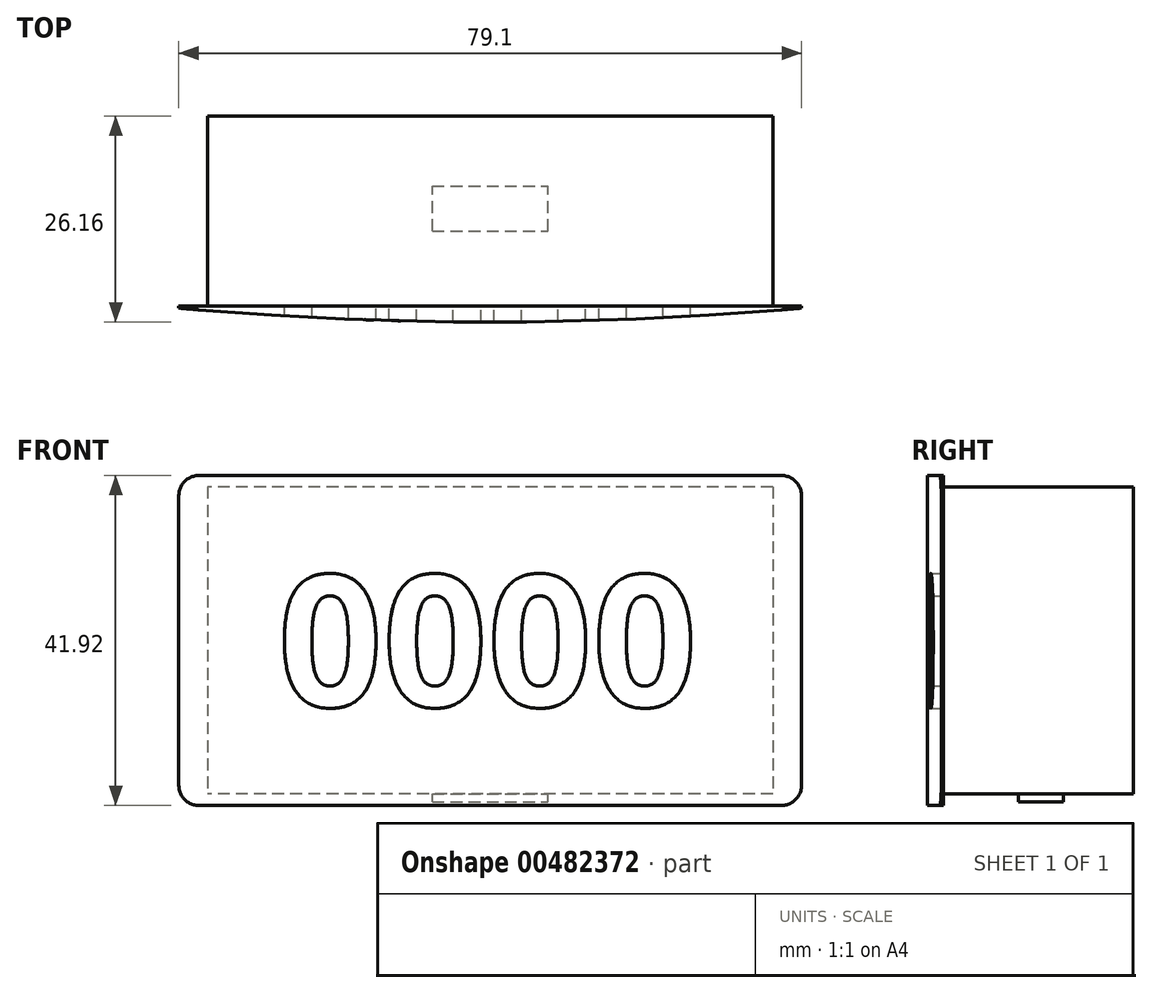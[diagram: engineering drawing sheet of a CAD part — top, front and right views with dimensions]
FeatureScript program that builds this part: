
annotation { "Feature Type Name" : "Feature", "Feature Type Description" : "" }
export const myFeature = defineFeature(function(context is Context, id is Id, definition is map)
    precondition{}
    {
        {
            var Q0;
            Q0=qCreatedBy(makeId("Front.planeOp"),FACE);
            var sketch = newSketch(context, id + "F0", { "sketchPlane" : qUnion([Q0])});
            skLineSegment(sketch, "E0.bottom", {"start": v(-39.55, 20.95) * mm, "end": v(39.55, 20.95) * mm});
            skLineSegment(sketch, "E0.top", {"start": v(-39.55, -20.96) * mm, "end": v(39.55, -20.96) * mm});
            skLineSegment(sketch, "E0.left", {"start": v(-39.55, 20.95) * mm, "end": v(-39.55, -20.96) * mm});
            skLineSegment(sketch, "E0.right", {"start": v(39.55, 20.95) * mm, "end": v(39.55, -20.96) * mm});
            skPoint(sketch, "E0.middle", {"position": v(0, 0) * mm});
            skSolve(sketch);
        }
        {
            var Q0;
            Q0 = qSketchRegion(id + "F0", true);
            extrude(context, id + "F1", {"entities" : qUnion([Q0]), "depth" : 2.03 * mm});
        }
        {
            var Q0;
            Q0=makeQuery(id+"F1.opExtrude","SWEPT_FACE",FACE,{"disambiguationData":[OSD([sQuery(id+"F0.wireOp",EDGE,"E0.top")])]});
            var sketch = newSketch(context, id + "F2", { "sketchPlane" : qUnion([Q0])});
            skCircle(sketch, "E1", {"center": v(0, -442.47) * mm, "radius": 444.5 * mm});
            skSolve(sketch);
        }
        {
            var Q0;
            Q0 = qSketchRegion(id + "F2", true);
            extrude(context, id + "F3", {"entities" : qUnion([Q0]), "operationType" : NewBodyOperationType.INTERSECT, "oppositeDirection" : true, "depth" : 50.8 * mm});
        }
        {
            var Q0;
            Q0=makeQuery(id+"F1.opExtrude","CAP_FACE",FACE,{"disambiguationData":[OSD([sQuery(id+"F0.wireOp",EDGE,"E0.bottom"),sQuery(id+"F0.wireOp",EDGE,"E0.top"),sQuery(id+"F0.wireOp",EDGE,"E0.left"),sQuery(id+"F0.wireOp",EDGE,"E0.right")])],"isStart":true});
            var sketch = newSketch(context, id + "F4", { "sketchPlane" : qUnion([Q0])});
            skLineSegment(sketch, "E2.bottom", {"start": v(-35.92, 19.5) * mm, "end": v(35.92, 19.5) * mm});
            skLineSegment(sketch, "E2.top", {"start": v(-35.92, -19.5) * mm, "end": v(35.92, -19.5) * mm});
            skLineSegment(sketch, "E2.left", {"start": v(-35.92, 19.5) * mm, "end": v(-35.92, -19.5) * mm});
            skLineSegment(sketch, "E2.right", {"start": v(35.92, 19.5) * mm, "end": v(35.92, -19.5) * mm});
            skPoint(sketch, "E2.middle", {"position": v(0, 0) * mm});
            skSolve(sketch);
        }
        {
            var Q0;
            Q0 = qSketchRegion(id + "F4", true);
            extrude(context, id + "F5", {"entities" : qUnion([Q0]), "operationType" : NewBodyOperationType.ADD, "depth" : 24.13 * mm});
        }
        {
            var Q0;
            Q0=makeQuery(id+"F5.opExtrude","SWEPT_FACE",FACE,{"disambiguationData":[OSD([sQuery(id+"F4.wireOp",EDGE,"E2.top")])]});
            var sketch = newSketch(context, id + "F6", { "sketchPlane" : qUnion([Q0])});
            skLineSegment(sketch, "E3.bottom", {"start": v(-7.33, -9.53) * mm, "end": v(7.33, -9.52) * mm});
            skLineSegment(sketch, "E3.top", {"start": v(-7.33, -15.24) * mm, "end": v(7.33, -15.24) * mm});
            skLineSegment(sketch, "E3.left", {"start": v(-7.33, -9.53) * mm, "end": v(-7.33, -15.24) * mm});
            skLineSegment(sketch, "E3.right", {"start": v(7.33, -9.52) * mm, "end": v(7.33, -15.24) * mm});
            skPoint(sketch, "E3.middle", {"position": v(0, -12.38) * mm});
            skSolve(sketch);
        }
        {
            var Q0;
            Q0 = qSketchRegion(id + "F6", true);
            extrude(context, id + "F7", {"entities" : qUnion([Q0]), "operationType" : NewBodyOperationType.ADD, "depth" : 1.02 * mm});
        }
        {
            var Q0;
            Q0=qCreatedBy(makeId("Front.planeOp"),FACE);
            var sketch = newSketch(context, id + "F8", { "sketchPlane" : qUnion([Q0])});
            skText(sketch, "E4", { "text": "0000", "fontName": "OpenSans-Bold.ttf"});
            const initialGuessF8  = {"E4": [-0.02699, -0.0084, 1, 0, 0.0168]};
            skSetInitialGuess(sketch, initialGuessF8);
            skSolve(sketch);
        }
        {
            var Q0;
            Q0 = qSketchRegion(id + "F8", true);
            extrude(context, id + "F9", {"entities" : qUnion([Q0]), "operationType" : NewBodyOperationType.REMOVE, "depth" : 4.24 * mm});
        }
        {
            var Q0;
            Q0=makeQuery(id+"F1.opExtrude","SWEPT_EDGE",EDGE,{"disambiguationData":[OSD([sQuery(id+"F0.wireOp",EDGE,"E0.bottom"),sQuery(id+"F0.wireOp",EDGE,"E0.left")])]});
            var Q1;
            Q1=makeQuery(id+"F1.opExtrude","SWEPT_EDGE",EDGE,{"disambiguationData":[OSD([sQuery(id+"F0.wireOp",EDGE,"E0.bottom"),sQuery(id+"F0.wireOp",EDGE,"E0.right")])]});
            var Q2;
            Q2=makeQuery(id+"F1.opExtrude","SWEPT_EDGE",EDGE,{"disambiguationData":[OSD([sQuery(id+"F0.wireOp",EDGE,"E0.top"),sQuery(id+"F0.wireOp",EDGE,"E0.right")])]});
            var Q3;
            Q3=makeQuery(id+"F1.opExtrude","SWEPT_EDGE",EDGE,{"disambiguationData":[OSD([sQuery(id+"F0.wireOp",EDGE,"E0.top"),sQuery(id+"F0.wireOp",EDGE,"E0.left")])]});
            fillet(context, id + "F10", {"entities" : qUnion([Q0, Q1, Q2, Q3]), "radius" : 2.54 * mm, "tangentPropagation" : true, "allowEdgeOverflow" : false});
        }
    });
